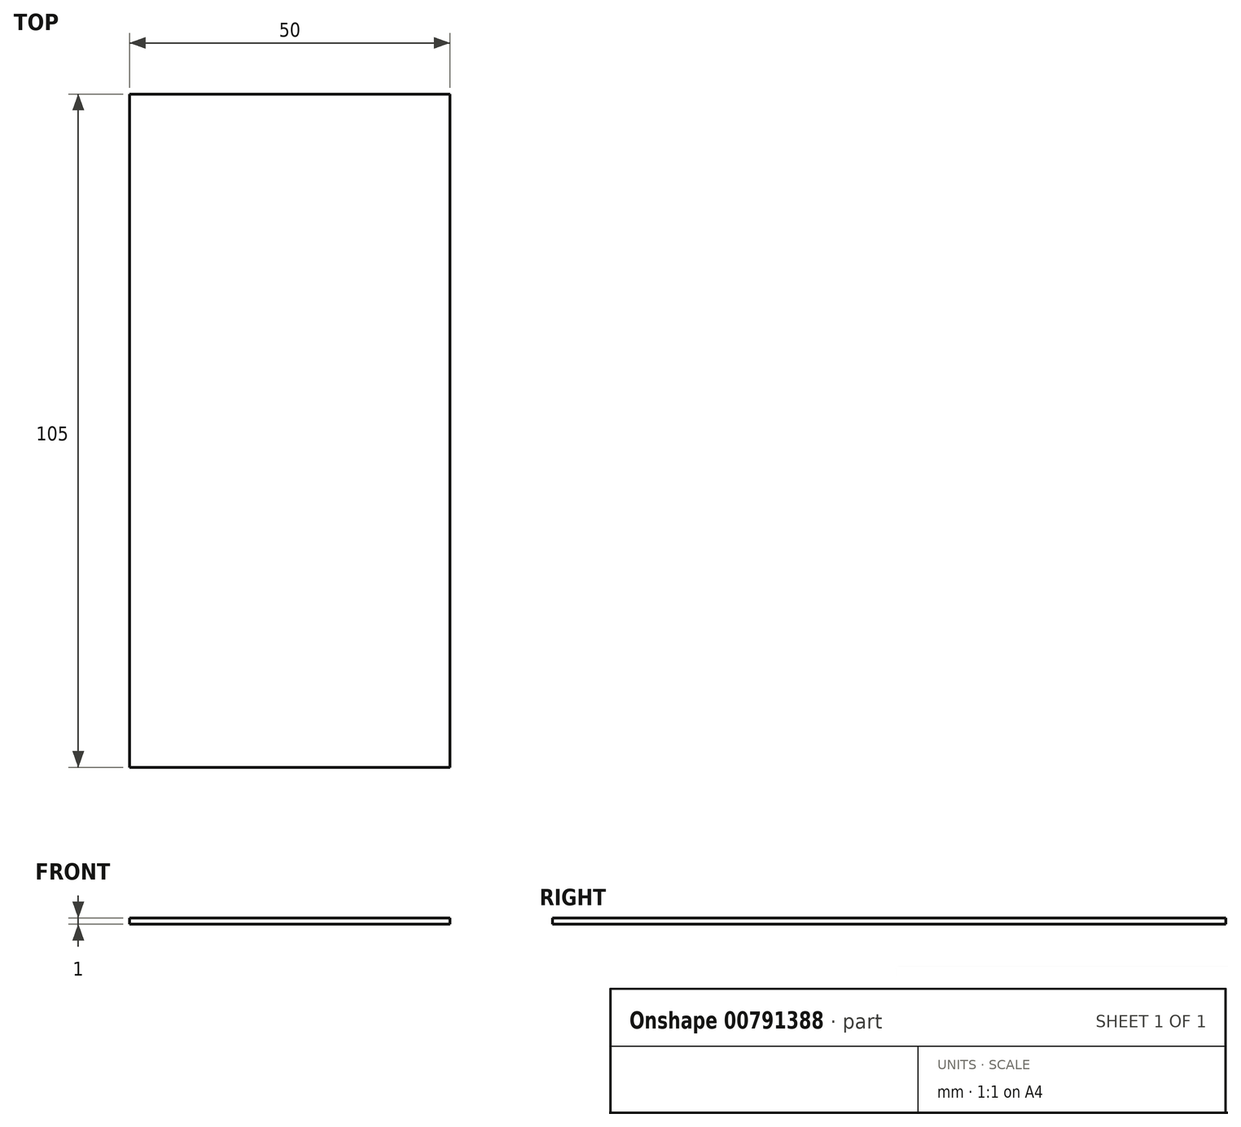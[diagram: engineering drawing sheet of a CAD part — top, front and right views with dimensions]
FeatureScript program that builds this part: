
annotation { "Feature Type Name" : "Feature", "Feature Type Description" : "" }
export const myFeature = defineFeature(function(context is Context, id is Id, definition is map)
    precondition{}
    {
        {
            var Q0;
            Q0=qCreatedBy(makeId("Top.planeOp"),FACE);
            var sketch = newSketch(context, id + "F0", { "sketchPlane" : qUnion([Q0])});
            skLineSegment(sketch, "E0.bottom", {"start": v(25, 52.5) * mm, "end": v(-25, 52.5) * mm});
            skLineSegment(sketch, "E0.top", {"start": v(25, -52.5) * mm, "end": v(-25, -52.5) * mm});
            skLineSegment(sketch, "E0.left", {"start": v(25, 52.5) * mm, "end": v(25, -52.5) * mm});
            skLineSegment(sketch, "E0.right", {"start": v(-25, 52.5) * mm, "end": v(-25, -52.5) * mm});
            skPoint(sketch, "E0.middle", {"position": v(0, 0) * mm});
            skSolve(sketch);
        }
        {
            var Q0;
            Q0=makeQuery(id+"F0.imprint","IMPRINT",FACE,{"disambiguationData":[TD([[makeQuery(id+"F0.imprint","IMPRINT",EDGE,{"derivedFrom":sQuery(id+"F0.wireOp",EDGE,"E0.bottom")}),1.0]])]});
            extrude(context, id + "F1", {"entities" : qUnion([Q0]), "depth" : 1 * mm, "offsetDistance" : 25.4 * mm});
        }
    });
